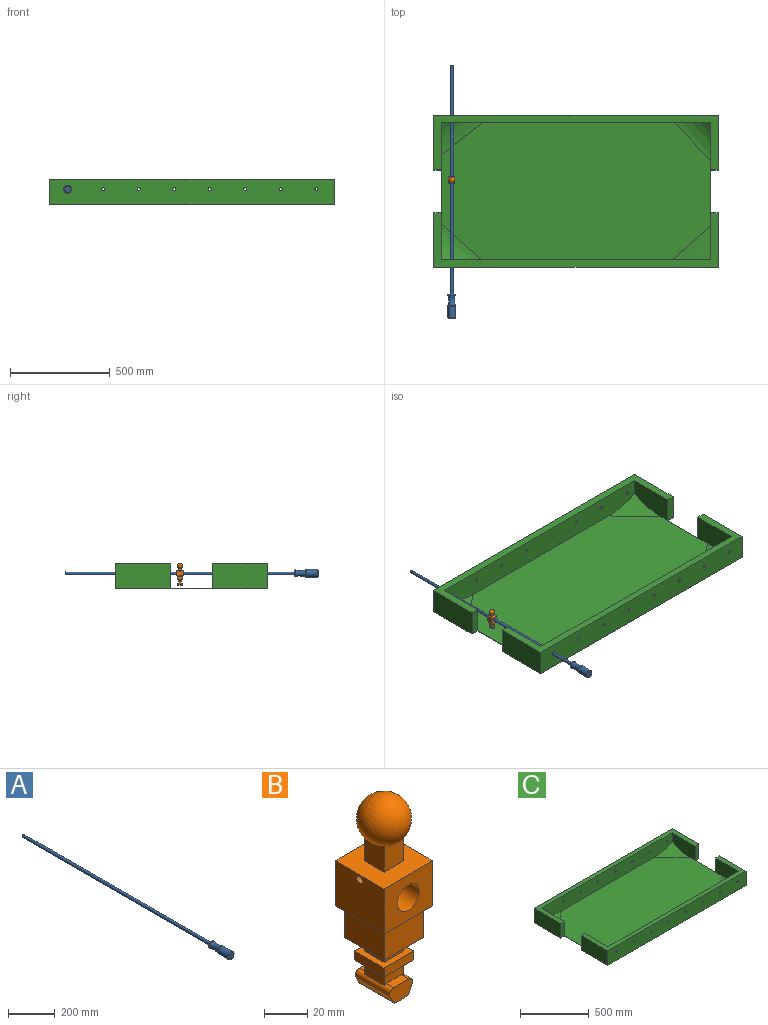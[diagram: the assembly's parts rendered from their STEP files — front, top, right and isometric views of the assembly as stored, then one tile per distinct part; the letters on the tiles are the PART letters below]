
ASSEMBLY  parts=3 mates=2
PART A: 9 faces, bbox 42.1x1262.1x42.1 mm
  f0: cylinder r=6.99mm len=1143mm, axis (0,-1,0), area 50164mm2, adj f1,f2
  f1: plane 13.97x13.97mm, normal (0,1,0), area 153.3mm2, adj f0
  f2: plane 28.81x28.81mm, normal (0,1,0), area 498.6mm2, adj f0,f8
  f3: plane 31.31x31.31mm, normal (0,-1,0), area 769.8mm2, adj f4
  f4: torus R=15.65mm, axis (0,-1,0), area 679.8mm2, adj f3,f5
  f5: cylinder r=19.46mm len=56.01mm, axis (0,-1,0), area 6850.1mm2, adj f4,f6
  f6: torus R=6.76mm, axis (0,-1,0), area 354.3mm2, adj f5,f7
  f7: revolved ~51.43x38.26mm, area 5189.6mm2, adj f6,f8
  f8: torus R=14.41mm, axis (0,-1,0), area 771.1mm2, adj f2,f7
PART B: 48 faces, bbox 31.8x31.8x109.2 mm
  f0: plane 9.93x4.76mm, normal (0,0,1), area 47.3mm2, adj f27,f31,f43,f46
  f1: plane 25.4x25.4mm, normal (0,0,-1), area 483.9mm2, adj f14,f15,f16,f17,f18,f19,f20,f21
  f2: plane 31.75x31.75mm, normal (0,0,-1), area 645.2mm2, adj f4,f6,f7,f8,f9,f10,f11,f12
  f3: plane 31.75x31.75mm, normal (0,0,1), area 846.8mm2, adj f4,f6,f7,f8,f38,f39,f40,f41
  f4: plane 31.75x25.4mm, normal (-1,0,0), area 795mm2, adj f2,f3,f7,f8,f47
  f5: cylinder r=7.14mm len=31.75mm, axis (0,1,0), area 1425.1mm2, adj f7,f8
  f6: plane 31.75x25.4mm, normal (1,0,0), area 795mm2, adj f2,f3,f7,f8,f47
  f7: plane 31.75x25.4mm, normal (0,-1,0), area 646.1mm2, adj f2,f3,f4,f5,f6
  f8: plane 31.75x25.4mm, normal (0,1,0), area 646.1mm2, adj f2,f3,f4,f5,f6
  f9: plane 19.05x2.54mm, normal (1,0,0), area 48.4mm2, adj f2,f11,f12,f13
  f10: plane 19.05x2.54mm, normal (-1,0,0), area 48.4mm2, adj f2,f11,f12,f13
  f11: plane 19.05x2.54mm, normal (0,-1,0), area 48.4mm2, adj f2,f9,f10,f13
  f12: plane 19.05x2.54mm, normal (0,1,0), area 48.4mm2, adj f2,f9,f10,f13
  f13: plane 25.4x25.4mm, normal (0,0,1), area 282.3mm2, adj f9,f10,f11,f12,f14,f15,f16,f17
  f14: plane 25.4x15.24mm, normal (-1,0,0), area 387.1mm2, adj f1,f13,f16,f17
  f15: plane 25.4x15.24mm, normal (1,0,0), area 387.1mm2, adj f1,f13,f16,f17
  f16: plane 25.4x15.24mm, normal (0,-1,0), area 387.1mm2, adj f1,f13,f14,f15
  f17: plane 25.4x15.24mm, normal (0,1,0), area 387.1mm2, adj f1,f13,f14,f15
  f18: plane 12.7x7.62mm, normal (1,0,0), area 96.8mm2, adj f1,f20,f21,f34
  f19: plane 12.7x7.62mm, normal (-1,0,0), area 96.8mm2, adj f1,f20,f21,f34
  f20: plane 12.7x7.62mm, normal (0,-1,0), area 96.8mm2, adj f1,f18,f19,f34
  f21: plane 12.7x7.62mm, normal (0,1,0), area 96.8mm2, adj f1,f18,f19,f34
  f22: plane 9.93x4.76mm, normal (0,0,1), area 47.3mm2, adj f26,f30,f43,f46
  f23: plane 22.23x4.12mm, normal (-0.91,0,-0.41), area 100.4mm2, adj f26,f27,f43,f44
  f24: plane 22.23x6.24mm, normal (0,0,-1), area 138.6mm2, adj f26,f27,f44,f45
  f25: plane 22.23x4.12mm, normal (0.91,0,-0.41), area 100.4mm2, adj f26,f27,f45,f46
  f26: plane 15.01x9.2mm, normal (0,-1,0), area 117.6mm2, adj f22,f23,f24,f25,f43,f44,f45,f46
  f27: plane 15.01x9.2mm, normal (0,1,0), area 117.6mm2, adj f0,f23,f24,f25,f43,f44,f45,f46
  f28: plane 12.7x8.03mm, normal (1,0,0), area 102mm2, adj f30,f31,f32,f46
  f29: plane 12.7x8.03mm, normal (-1,0,0), area 102mm2, adj f30,f31,f32,f43
  f30: plane 12.7x8.03mm, normal (0,-1,0), area 97.1mm2, adj f22,f28,f29,f32,f43,f46
  f31: plane 12.7x8.03mm, normal (0,1,0), area 97.1mm2, adj f0,f28,f29,f32,f43,f46
  f32: plane 19.05x19.05mm, normal (0,0,-1), area 201.6mm2, adj f28,f29,f30,f31,f33,f35,f36,f37
  f33: plane 19.05x5.08mm, normal (1,0,0), area 96.8mm2, adj f32,f34,f36,f37
  f34: plane 19.05x19.05mm, normal (0,0,1), area 201.6mm2, adj f18,f19,f20,f21,f33,f35,f36,f37
  f35: plane 19.05x5.08mm, normal (-1,0,0), area 96.8mm2, adj f32,f34,f36,f37
  f36: plane 19.05x5.08mm, normal (0,-1,0), area 96.8mm2, adj f32,f33,f34,f35
  f37: plane 19.05x5.08mm, normal (0,1,0), area 96.8mm2, adj f32,f33,f34,f35
  f38: plane 14.84x12.7mm, normal (0,1,0), area 171mm2, adj f3,f39,f40,f42
  f39: plane 14.84x12.7mm, normal (-1,0,0), area 171mm2, adj f3,f38,f41,f42
  f40: plane 14.84x12.7mm, normal (1,0,0), area 171mm2, adj f3,f38,f41,f42
  f41: plane 14.84x12.7mm, normal (0,-1,0), area 171mm2, adj f3,f39,f40,f42
  f42: sphere r=12.7mm, area 1849mm2, adj f38,f39,f40,f41
  f43: cylinder r=2.54mm len=22.23mm, axis (0,1,0), area 93.9mm2, adj f0,f22,f23,f26,f27,f29,f30,f31
  f44: cylinder r=2.54mm len=22.23mm, axis (0,-1,0), area 64.9mm2, adj f23,f24,f26,f27
  f45: cylinder r=2.54mm len=22.23mm, axis (0,1,0), area 64.9mm2, adj f24,f25,f26,f27
  f46: cylinder r=2.54mm len=22.23mm, axis (0,-1,0), area 93.9mm2, adj f0,f22,f25,f26,f27,f28,f30,f31
  f47: cylinder r=1.91mm len=31.75mm, axis (1,0,0), area 380mm2, adj f4,f6
PART C: 42 faces, bbox 1422.4x762x129.5 mm
  f0: plane 1346.2x127mm, normal (0,1,0), area 164285.3mm2, adj f1,f4,f5,f6,f19,f20,f21,f22
  f1: plane 236.54x127mm, normal (1,0,0), area 27501.8mm2, adj f0,f4,f5,f18,f39
  f2: plane 236.54x127mm, normal (1,0,0), area 27471.6mm2, adj f5,f11,f14,f17,f38
  f3: plane 274.64x129.54mm, normal (-1,0,0), area 35576.5mm2, adj f4,f10,f18,f35
  f4: plane 1422.4x274.64mm, normal (0,0,1), area 72217.6mm2, adj f0,f1,f3,f6,f7,f10,f16,f18
  f5: plane 1346.2x685.8mm, normal (0,0,1), area 855669.1mm2, adj f0,f1,f2,f6,f11,f12,f36,f37
  f6: plane 236.54x127mm, normal (-1,0,0), area 27948.7mm2, adj f0,f4,f5,f16,f40
  f7: plane 274.64x129.54mm, normal (1,0,0), area 35576.5mm2, adj f4,f10,f16,f35
  f8: plane 1422.4x129.54mm, normal (0,1,0), area 182798.4mm2, adj f9,f13,f14,f27,f28,f29,f30,f31
  f9: plane 274.64x129.54mm, normal (-1,0,0), area 35576.5mm2, adj f8,f14,f17,f35
  f10: plane 1422.4x129.54mm, normal (0,-1,0), area 182798.4mm2, adj f3,f4,f7,f19,f20,f21,f22,f23
  f11: plane 1346.21x127.01mm, normal (0,-1,0), area 163359.6mm2, adj f2,f5,f12,f14,f27,f28,f29,f30
  f12: plane 236.54x127mm, normal (-1,0,0), area 27142.8mm2, adj f5,f11,f14,f15,f41
  f13: plane 274.64x129.54mm, normal (1,0,0), area 35576.5mm2, adj f8,f14,f15,f35
  f14: plane 1422.4x274.64mm, normal (0,0,1), area 72217.6mm2, adj f2,f8,f9,f11,f12,f13,f15,f17
  f15: plane 129.54x38.1mm, normal (0,-1,0), area 4935.5mm2, adj f12,f13,f14,f35,f36
  f16: plane 129.54x38.1mm, normal (0,1,0), area 4935.5mm2, adj f4,f6,f7,f35,f36
  f17: plane 129.54x38.1mm, normal (0,-1,0), area 4935.5mm2, adj f2,f9,f14,f35,f37
  f18: plane 129.54x38.1mm, normal (0,1,0), area 4935.5mm2, adj f1,f3,f4,f35,f37
  f19: cylinder r=7.62mm len=38.1mm, axis (0,-1,0), area 1824.1mm2, adj f0,f10
  f20: cylinder r=7.62mm len=38.1mm, axis (0,-1,0), area 1824.1mm2, adj f0,f10
  f21: cylinder r=7.62mm len=38.1mm, axis (0,-1,0), area 1824.1mm2, adj f0,f10
  f22: cylinder r=7.62mm len=38.1mm, axis (0,-1,0), area 1824.1mm2, adj f0,f10
  f23: cylinder r=7.62mm len=38.1mm, axis (0,-1,0), area 1824.1mm2, adj f0,f10
  f24: cylinder r=7.62mm len=38.1mm, axis (0,-1,0), area 1824.1mm2, adj f0,f10
  f25: cylinder r=7.62mm len=38.1mm, axis (0,-1,0), area 1824.1mm2, adj f0,f10
  f26: cylinder r=7.62mm len=38.1mm, axis (0,-1,0), area 1824.1mm2, adj f0,f10
  f27: cylinder r=7.62mm len=38.1mm, axis (0,-1,0), area 1824.1mm2, adj f8,f11
  f28: cylinder r=7.62mm len=38.1mm, axis (0,-1,0), area 1824.1mm2, adj f8,f11
  f29: cylinder r=7.62mm len=38.1mm, axis (0,-1,0), area 1824.1mm2, adj f8,f11
  f30: cylinder r=7.62mm len=38.1mm, axis (0,-1,0), area 1824.1mm2, adj f8,f11
  f31: cylinder r=7.62mm len=38.1mm, axis (0,-1,0), area 1824.1mm2, adj f8,f11
  f32: cylinder r=7.62mm len=38.1mm, axis (0,-1,0), area 1824.1mm2, adj f8,f11
  f33: cylinder r=7.62mm len=38.1mm, axis (0,-1,0), area 1824.1mm2, adj f8,f11
  f34: cylinder r=7.62mm len=38.1mm, axis (0,-1,0), area 1824.1mm2, adj f8,f11
  f35: plane 1422.4x762mm, normal (0,0,-1), area 1067659.2mm2, adj f3,f7,f8,f9,f10,f13,f15,f16
  f36: plane 212.73x2.54mm, normal (1,0,0), area 540.3mm2, adj f5,f15,f16,f35
  f37: plane 212.73x2.54mm, normal (-1,0,0), area 540.3mm2, adj f5,f17,f18,f35
  f38: bspline ~206.48x159.78mm, area 17291.2mm2, adj f2,f5,f11
  f39: bspline ~201.72x178.2mm, area 18578.7mm2, adj f0,f1,f5
  f40: bspline ~191.18x169.74mm, area 16671.5mm2, adj f0,f5,f6
  f41: bspline ~187.66x179.71mm, area 17561.3mm2, adj f5,f11,f12
PLACE A t=(-630,-517.27,-183.77)mm
PLACE B t=(-630,54.23,-147.25)mm
PLACE C t=(-7.7,-1.7,-259.97)mm
MATE fastened B.f5 <-> A.f0  axis (0,1,0) through (-630,54.23,-183.77)mm
MATE slider A.f0 <-> C.f26  axis (0,-1,0) through (-630,-517.27,-183.77)mm
